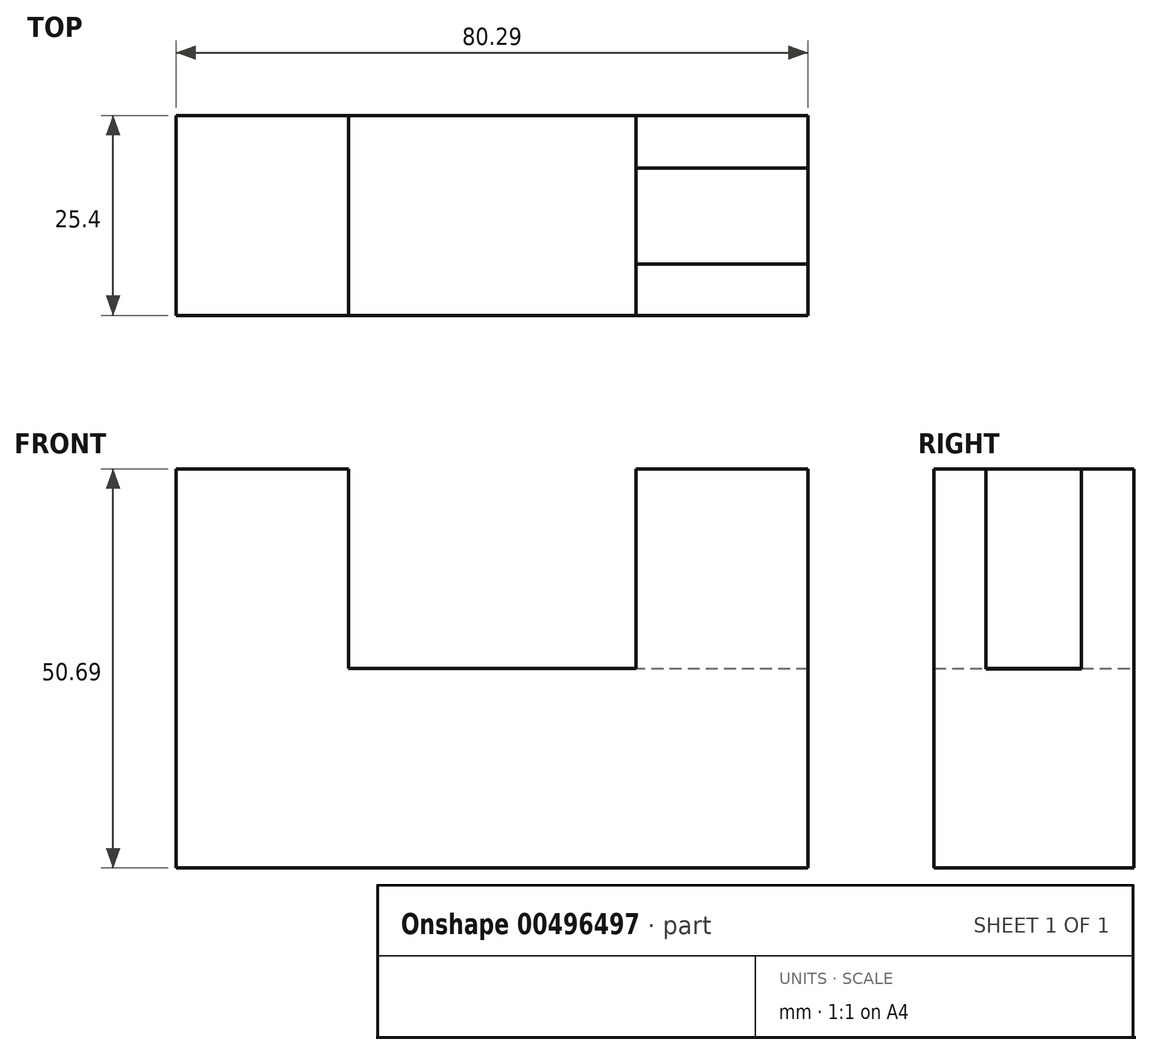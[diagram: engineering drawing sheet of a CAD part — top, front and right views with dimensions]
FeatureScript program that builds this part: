
annotation { "Feature Type Name" : "Feature", "Feature Type Description" : "" }
export const myFeature = defineFeature(function(context is Context, id is Id, definition is map)
    precondition{}
    {
        {
            var Q0;
            Q0=qCreatedBy(makeId("Front.planeOp"),FACE);
            var sketch = newSketch(context, id + "F0", { "sketchPlane" : qUnion([Q0])});
            skLineSegment(sketch, "E0.bottom", {"start": v(0, 0) * mm, "end": v(80.29, 0) * mm});
            skLineSegment(sketch, "E0.top", {"start": v(0, 50.69) * mm, "end": v(21.9, 50.69) * mm});
            skLineSegment(sketch, "E0.left", {"start": v(0, 0) * mm, "end": v(0, 50.69) * mm});
            skLineSegment(sketch, "E0.right", {"start": v(80.29, 0) * mm, "end": v(80.29, 50.69) * mm});
            skPoint(sketch, "E1.oppositeSnap0", {"position": v(0, 25.34) * mm});
            skLineSegment(sketch, "E1.top", {"start": v(21.9, 25.34) * mm, "end": v(58.4, 25.34) * mm});
            skLineSegment(sketch, "E1.left", {"start": v(21.9, 50.69) * mm, "end": v(21.9, 25.34) * mm});
            skLineSegment(sketch, "E1.right", {"start": v(58.4, 50.69) * mm, "end": v(58.4, 25.34) * mm});
            skLineSegment(sketch, "E2.trimOffspring", {"start": v(58.4, 50.69) * mm, "end": v(80.29, 50.69) * mm});
            skSolve(sketch);
        }
        {
            var Q0;
            Q0=makeQuery(id+"F0.imprint","IMPRINT",FACE,{"disambiguationData":[TD([[makeQuery(id+"F0.imprint","IMPRINT",EDGE,{"derivedFrom":sQuery(id+"F0.wireOp",EDGE,"E0.bottom")}),1.0]])]});
            extrude(context, id + "F1", {"entities" : qUnion([Q0]), "depth" : 25.4 * mm});
        }
        {
            var Q0;
            Q0=makeQuery(id+"F1.opExtrude","SWEPT_FACE",FACE,{"disambiguationData":[OSD([sQuery(id+"F0.wireOp",EDGE,"E2.trimOffspring")])]});
            var sketch = newSketch(context, id + "F2", { "sketchPlane" : qUnion([Q0])});
            skLineSegment(sketch, "E3.bottom", {"start": v(80.29, -18.85) * mm, "end": v(58.4, -18.85) * mm});
            skLineSegment(sketch, "E3.top", {"start": v(80.29, -6.66) * mm, "end": v(58.4, -6.66) * mm});
            skLineSegment(sketch, "E3.left", {"start": v(80.29, -18.85) * mm, "end": v(80.29, -6.66) * mm});
            skLineSegment(sketch, "E3.right", {"start": v(58.4, -18.85) * mm, "end": v(58.4, -6.66) * mm});
            skSolve(sketch);
        }
        {
            var Q0;
            Q0=makeQuery(id+"F2.imprint","IMPRINT",FACE,{"disambiguationData":[TD([[makeQuery(id+"F2.imprint","IMPRINT",EDGE,{"derivedFrom":sQuery(id+"F2.wireOp",EDGE,"E3.bottom")}),-1.0]])]});
            extrude(context, id + "F3", {"entities" : qUnion([Q0]), "operationType" : NewBodyOperationType.REMOVE, "oppositeDirection" : true, "depth" : 25.4 * mm});
        }
    });
